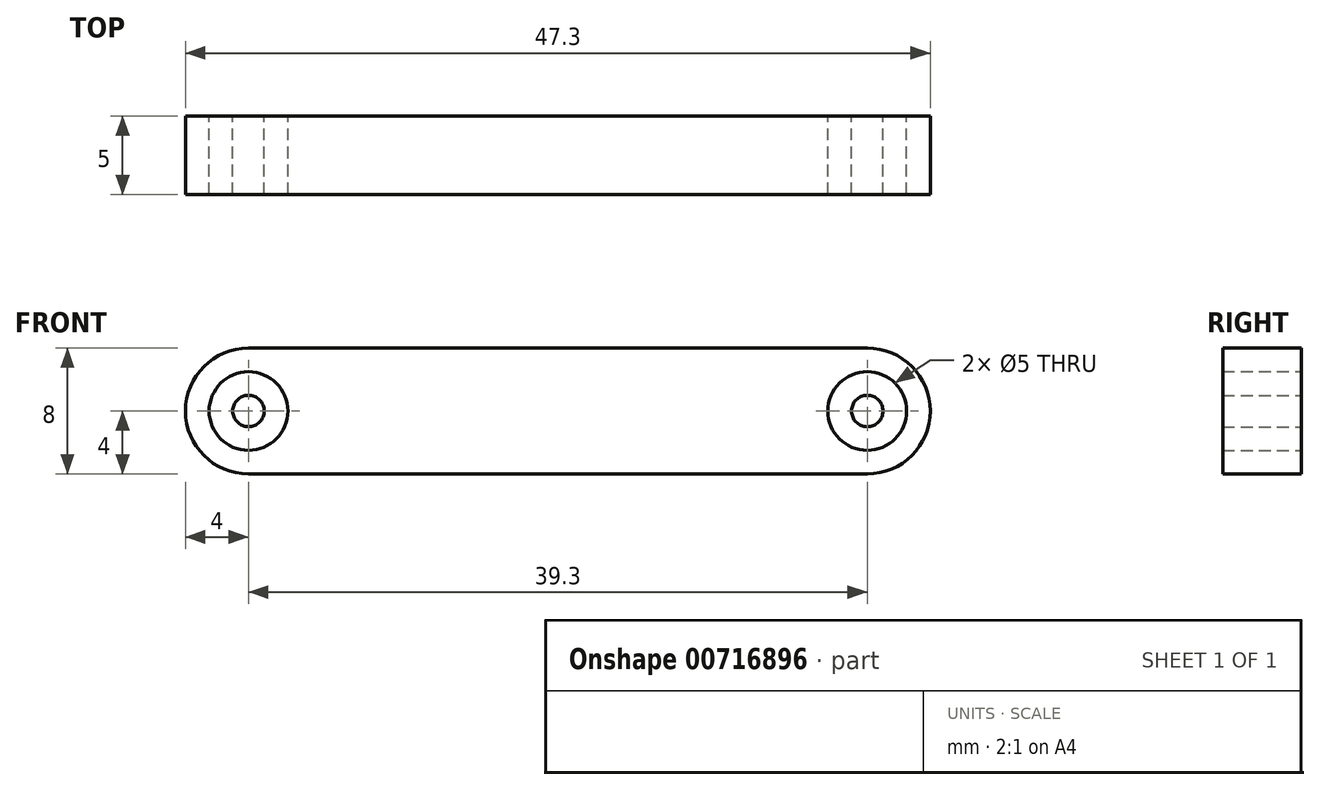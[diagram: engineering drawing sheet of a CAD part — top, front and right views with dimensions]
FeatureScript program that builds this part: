
annotation { "Feature Type Name" : "Feature", "Feature Type Description" : "" }
export const myFeature = defineFeature(function(context is Context, id is Id, definition is map)
    precondition{}
    {
        {
            var Q0;
            Q0=qCreatedBy(makeId("Front.planeOp"),FACE);
            var sketch = newSketch(context, id + "F0", { "sketchPlane" : qUnion([Q0])});
            skArc(sketch, "E0", {"start": v(0, -4) * mm, "mid": v(4, 0) * mm, "end": v(0, 4) * mm});
            skArc(sketch, "E1", {"start": v(-39.3, 4) * mm, "mid": v(-43.3, 0) * mm, "end": v(-39.3, -4) * mm});
            skLineSegment(sketch, "E2", {"start": v(0, 4) * mm, "end": v(-39.3, 4) * mm});
            skLineSegment(sketch, "E3", {"start": v(0, -4) * mm, "end": v(-39.3, -4) * mm});
            skCircle(sketch, "E4", {"center": v(0, 0) * mm, "radius": 1 * mm});
            skCircle(sketch, "E5", {"center": v(0, 0) * mm, "radius": 2.5 * mm});
            skCircle(sketch, "E6", {"center": v(-39.3, 0) * mm, "radius": 2.5 * mm});
            skCircle(sketch, "E7", {"center": v(-39.3, 0) * mm, "radius": 1 * mm});
            skSolve(sketch);
        }
        {
            var Q0;
            Q0 = qSketchRegion(id + "F0", true);
            var Q1;
            Q1=makeQuery(id+"F0.imprint","IMPRINT",FACE,{"disambiguationData":[TD([[makeQuery(id+"F0.imprint","IMPRINT",EDGE,{"derivedFrom":sQuery(id+"F0.wireOp",EDGE,"E7")}),1.0]])]});
            var Q2;
            Q2=makeQuery(id+"F0.imprint","IMPRINT",FACE,{"disambiguationData":[TD([[makeQuery(id+"F0.imprint","IMPRINT",EDGE,{"derivedFrom":sQuery(id+"F0.wireOp",EDGE,"E4")}),1.0]])]});
            extrude(context, id + "F1", {"entities" : qUnion([Q0, Q1, Q2]), "depth" : 5 * mm, "offsetDistance" : 25.4 * mm});
        }
    });
